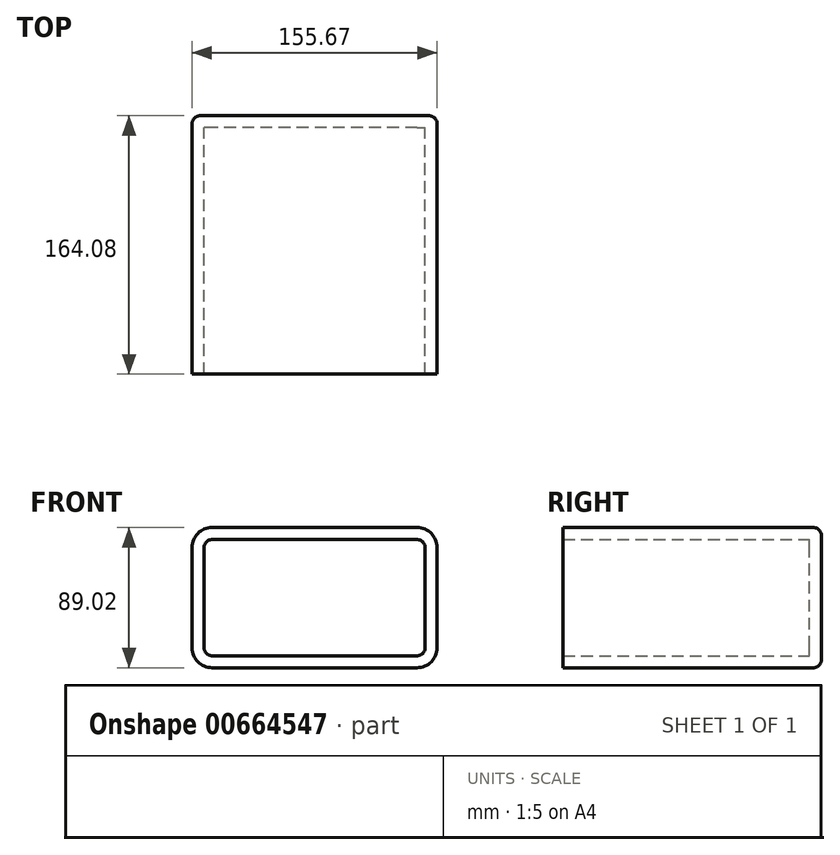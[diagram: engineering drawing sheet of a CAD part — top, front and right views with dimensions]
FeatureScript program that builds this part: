
annotation { "Feature Type Name" : "Feature", "Feature Type Description" : "" }
export const myFeature = defineFeature(function(context is Context, id is Id, definition is map)
    precondition{}
    {
        {
            var Q0;
            Q0=qCreatedBy(makeId("Front.planeOp"),FACE);
            var sketch = newSketch(context, id + "F0", { "sketchPlane" : qUnion([Q0])});
            skLineSegment(sketch, "E0", {"start": v(-14.5, 54.98) * mm, "end": v(141.17, 54.98) * mm});
            skLineSegment(sketch, "E1", {"start": v(141.17, 54.98) * mm, "end": v(141.17, -34.04) * mm});
            skLineSegment(sketch, "E2", {"start": v(141.17, -34.04) * mm, "end": v(-14.5, -34.04) * mm});
            skLineSegment(sketch, "E3", {"start": v(-14.5, -34.04) * mm, "end": v(-14.5, 54.98) * mm});
            skSolve(sketch);
        }
        {
            var Q0;
            Q0=makeQuery(id+"F0.imprint","IMPRINT",FACE,{"disambiguationData":[TD([[makeQuery(id+"F0.imprint","IMPRINT",EDGE,{"derivedFrom":sQuery(id+"F0.wireOp",EDGE,"E0")}),-1.0]])]});
            extrude(context, id + "F1", {"entities" : qUnion([Q0]), "endBound" : BoundingType.SYMMETRIC, "depth" : 164.08 * mm, "offsetDistance" : 25.4 * mm});
        }
        {
            var Q0;
            Q0=makeQuery(id+"F1.opExtrude","SWEPT_EDGE",EDGE,{"disambiguationData":[OSD([sQuery(id+"F0.wireOp",EDGE,"E0"),sQuery(id+"F0.wireOp",EDGE,"E3")])]});
            var Q1;
            Q1=makeQuery(id+"F1.opExtrude","SWEPT_EDGE",EDGE,{"disambiguationData":[OSD([sQuery(id+"F0.wireOp",EDGE,"E2"),sQuery(id+"F0.wireOp",EDGE,"E3")])]});
            var Q2;
            Q2=makeQuery(id+"F1.opExtrude","SWEPT_EDGE",EDGE,{"disambiguationData":[OSD([sQuery(id+"F0.wireOp",EDGE,"E0"),sQuery(id+"F0.wireOp",EDGE,"E1")])]});
            var Q3;
            Q3=makeQuery(id+"F1.opExtrude","SWEPT_EDGE",EDGE,{"disambiguationData":[OSD([sQuery(id+"F0.wireOp",EDGE,"E1"),sQuery(id+"F0.wireOp",EDGE,"E2")])]});
            fillet(context, id + "F2", {"entities" : qUnion([Q0, Q1, Q2, Q3]), "radius" : 12.7 * mm, "tangentPropagation" : true, "allowEdgeOverflow" : false});
        }
        {
            var Q0;
            {var subQ0=sQuery(id+"F0.wireOp",EDGE,"E3");var subQ1=sQuery(id+"F0.wireOp",EDGE,"E2");Q0=makeQuery(id+"F2.opFillet","BLEND_EDGE",EDGE,{"blendedFrom":[makeQuery(id+"F1.opExtrude","SWEPT_EDGE",EDGE,{"disambiguationData":[OSD([subQ1,subQ0])]}),makeQuery(id+"F1.opExtrude","CAP_FACE",FACE,{"disambiguationData":[OSD([sQuery(id+"F0.wireOp",EDGE,"E0"),sQuery(id+"F0.wireOp",EDGE,"E1"),subQ1,subQ0])],"isStart":true})],"blendedInto":[makeQuery(id+"F1.opExtrude","CAP_FACE",FACE,{"disambiguationData":[OSD([sQuery(id+"F0.wireOp",EDGE,"E0"),sQuery(id+"F0.wireOp",EDGE,"E1"),subQ1,subQ0])],"isStart":true})]});}
            fillet(context, id + "F3", {"entities" : qUnion([Q0]), "radius" : 5.08 * mm, "tangentPropagation" : true, "allowEdgeOverflow" : false});
        }
        {
            var Q0;
            Q0=makeQuery(id+"F1.opExtrude","CAP_FACE",FACE,{"disambiguationData":[OSD([sQuery(id+"F0.wireOp",EDGE,"E0"),sQuery(id+"F0.wireOp",EDGE,"E1"),sQuery(id+"F0.wireOp",EDGE,"E2"),sQuery(id+"F0.wireOp",EDGE,"E3")])],"isStart":false});
            shell(context, id + "F4", {"entities" : qUnion([Q0]), "thickness" : 7.62 * mm});
        }
    });
